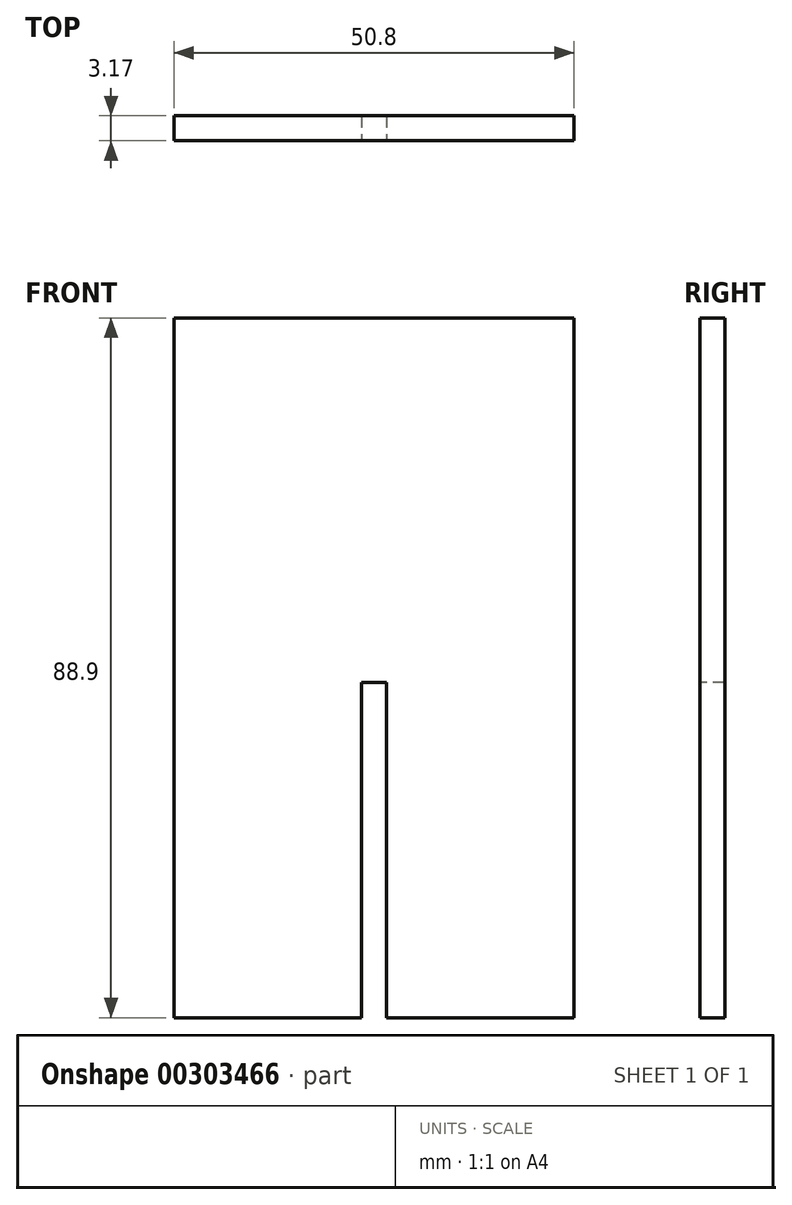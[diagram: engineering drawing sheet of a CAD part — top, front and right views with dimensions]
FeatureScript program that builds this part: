
annotation { "Feature Type Name" : "Feature", "Feature Type Description" : "" }
export const myFeature = defineFeature(function(context is Context, id is Id, definition is map)
    precondition{}
    {
        {
            var Q0;
            Q0=qCreatedBy(makeId("Front.planeOp"),FACE);
            var sketch = newSketch(context, id + "F0", { "sketchPlane" : qUnion([Q0])});
            skLineSegment(sketch, "E0.bottom", {"start": v(-25.4, 44.45) * mm, "end": v(25.4, 44.45) * mm});
            skLineSegment(sketch, "E0.top", {"start": v(-25.4, -44.45) * mm, "end": v(25.4, -44.45) * mm});
            skLineSegment(sketch, "E0.left", {"start": v(-25.4, 44.45) * mm, "end": v(-25.4, -44.45) * mm});
            skLineSegment(sketch, "E0.right", {"start": v(25.4, 44.45) * mm, "end": v(25.4, -44.45) * mm});
            skPoint(sketch, "E0.middle", {"position": v(0, 0) * mm});
            skSolve(sketch);
        }
        {
            var Q0;
            Q0 = qSketchRegion(id + "F0", true);
            extrude(context, id + "F1", {"entities" : qUnion([Q0]), "depth" : 3.17 * mm});
        }
        {
            var Q0;
            Q0=makeQuery(id+"F1.opExtrude","CAP_FACE",FACE,{"disambiguationData":[OSD([sQuery(id+"F0.wireOp",EDGE,"E0.bottom"),sQuery(id+"F0.wireOp",EDGE,"E0.top"),sQuery(id+"F0.wireOp",EDGE,"E0.left"),sQuery(id+"F0.wireOp",EDGE,"E0.right")])],"isStart":false});
            var sketch = newSketch(context, id + "F2", { "sketchPlane" : qUnion([Q0])});
            skLineSegment(sketch, "E1.bottom", {"start": v(1.59, -1.88) * mm, "end": v(-1.59, -1.88) * mm});
            skLineSegment(sketch, "E1.top", {"start": v(1.59, -44.74) * mm, "end": v(-1.59, -44.74) * mm});
            skLineSegment(sketch, "E1.left", {"start": v(1.59, -1.88) * mm, "end": v(1.59, -44.74) * mm});
            skLineSegment(sketch, "E1.right", {"start": v(-1.59, -1.88) * mm, "end": v(-1.59, -44.74) * mm});
            skPoint(sketch, "E1.middle", {"position": v(0, -23.3) * mm});
            skSolve(sketch);
        }
        {
            var Q0;
            Q0 = qSketchRegion(id + "F2", true);
            extrude(context, id + "F3", {"entities" : qUnion([Q0]), "operationType" : NewBodyOperationType.REMOVE, "oppositeDirection" : true, "depth" : 3.17 * mm});
        }
        {
            var Q0;
            Q0 = qSketchRegion(id + "F2", true);
            extrude(context, id + "F4", {"entities" : qUnion([Q0]), "operationType" : NewBodyOperationType.REMOVE, "oppositeDirection" : true, "depth" : 3.17 * mm});
        }
    });
